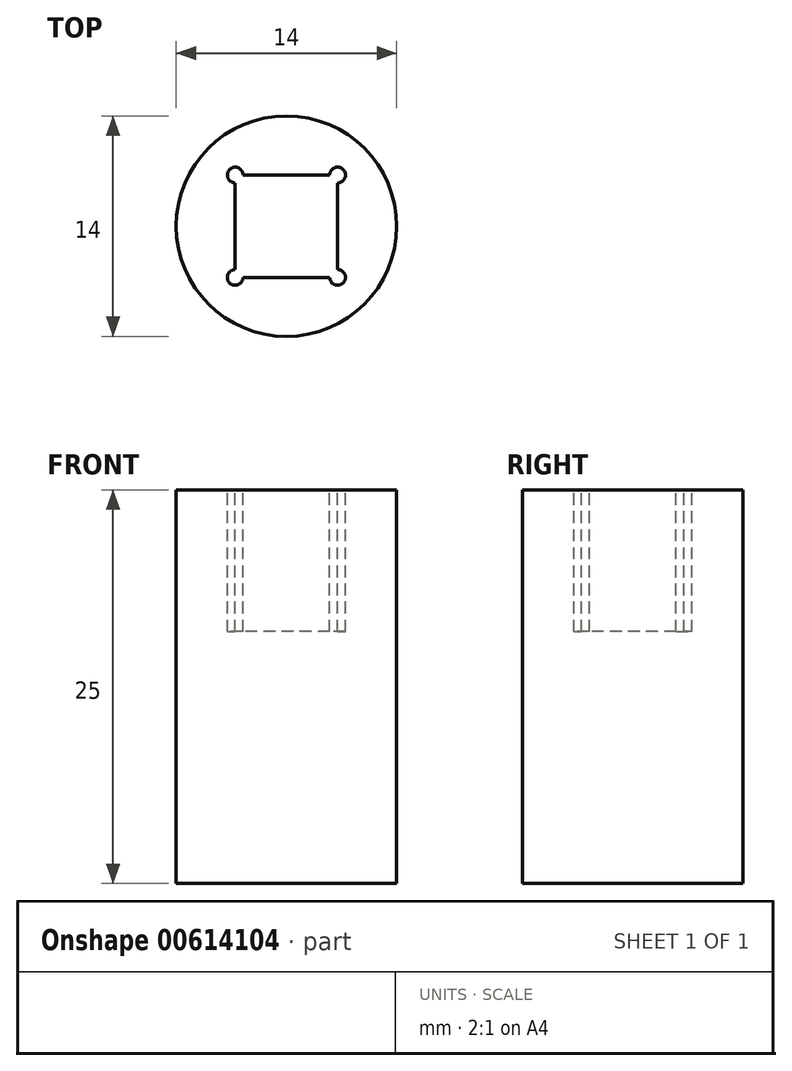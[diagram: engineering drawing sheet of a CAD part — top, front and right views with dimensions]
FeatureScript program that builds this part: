
annotation { "Feature Type Name" : "Feature", "Feature Type Description" : "" }
export const myFeature = defineFeature(function(context is Context, id is Id, definition is map)
    precondition{}
    {
        {
            var Q0;
            Q0=qCreatedBy(makeId("Top.planeOp"),FACE);
            var sketch = newSketch(context, id + "F0", { "sketchPlane" : qUnion([Q0])});
            skCircle(sketch, "E0", {"center": v(0, 0) * mm, "radius": 7 * mm});
            skSolve(sketch);
        }
        {
            var Q0;
            Q0=makeQuery(id+"F0.imprint","IMPRINT",FACE,{"disambiguationData":[TD([[makeQuery(id+"F0.imprint","IMPRINT",EDGE,{"derivedFrom":sQuery(id+"F0.wireOp",EDGE,"E0")}),1.0]])]});
            extrude(context, id + "F1", {"entities" : qUnion([Q0]), "depth" : 25 * mm, "offsetDistance" : 25 * mm});
        }
        {
            var Q0;
            Q0=makeQuery(id+"F1.opExtrude","CAP_FACE",FACE,{"disambiguationData":[OSD([sQuery(id+"F0.wireOp",EDGE,"E0")])],"isStart":false});
            var sketch = newSketch(context, id + "F2", { "sketchPlane" : qUnion([Q0])});
            skLineSegment(sketch, "E1.bottom", {"start": v(3.25, 3.25) * mm, "end": v(-3.25, 3.25) * mm});
            skLineSegment(sketch, "E1.top", {"start": v(3.25, -3.25) * mm, "end": v(-3.25, -3.25) * mm});
            skLineSegment(sketch, "E1.left", {"start": v(3.25, 3.25) * mm, "end": v(3.25, -3.25) * mm});
            skLineSegment(sketch, "E1.right", {"start": v(-3.25, 3.25) * mm, "end": v(-3.25, -3.25) * mm});
            skPoint(sketch, "E1.middle", {"position": v(0, 0) * mm});
            skCircle(sketch, "E2", {"center": v(-3.25, 3.25) * mm, "radius": 0.5 * mm});
            skCircle(sketch, "E3", {"center": v(3.25, 3.25) * mm, "radius": 0.5 * mm});
            skCircle(sketch, "E4", {"center": v(3.25, -3.25) * mm, "radius": 0.5 * mm});
            skCircle(sketch, "E5", {"center": v(-3.25, -3.25) * mm, "radius": 0.5 * mm});
            skSolve(sketch);
        }
        {
            var Q0;
            {var subQ5=sQuery(id+"F2.wireOp",EDGE,"E3");var subQ13=sQuery(id+"F2.wireOp",EDGE,"E1.bottom");var subQ14=makeQuery(id+"F2.imprint","INTERSECT",VERTEX,{"derivedFrom":[subQ13,subQ5]});Q0=makeQuery(id+"F2.imprint","IMPRINT",FACE,{"disambiguationData":[TD([[makeQuery(id+"F2.imprint","IMPRINT",EDGE,{"disambiguationData":[TD([[subQ14,-1.0]])],"derivedFrom":subQ13}),1.0]])]});}
            var Q1;
            {var subQ0=sQuery(id+"F2.wireOp",EDGE,"E1.right");var subQ1=sQuery(id+"F2.wireOp",EDGE,"E1.bottom");var subQ2=makeQuery(id+"F2.imprint","INTERSECT",VERTEX,{"derivedFrom":[subQ1,subQ0]});Q1=makeQuery(id+"F2.imprint","IMPRINT",FACE,{"disambiguationData":[TD([[makeQuery(id+"F2.imprint","IMPRINT",EDGE,{"disambiguationData":[TD([[subQ2,1.0]])],"derivedFrom":subQ1}),-1.0]])]});}
            var Q2;
            {var subQ0=sQuery(id+"F2.wireOp",EDGE,"E1.right");var subQ1=sQuery(id+"F2.wireOp",EDGE,"E1.top");var subQ2=makeQuery(id+"F2.imprint","INTERSECT",VERTEX,{"derivedFrom":[subQ1,subQ0]});Q2=makeQuery(id+"F2.imprint","IMPRINT",FACE,{"disambiguationData":[TD([[makeQuery(id+"F2.imprint","IMPRINT",EDGE,{"disambiguationData":[TD([[subQ2,1.0]])],"derivedFrom":subQ1}),1.0]])]});}
            var Q3;
            {var subQ0=sQuery(id+"F2.wireOp",EDGE,"E1.right");var subQ1=sQuery(id+"F2.wireOp",EDGE,"E1.top");var subQ2=makeQuery(id+"F2.imprint","INTERSECT",VERTEX,{"derivedFrom":[subQ1,subQ0]});Q3=makeQuery(id+"F2.imprint","IMPRINT",FACE,{"disambiguationData":[TD([[makeQuery(id+"F2.imprint","IMPRINT",EDGE,{"disambiguationData":[TD([[subQ2,1.0]])],"derivedFrom":subQ1}),-1.0]])]});}
            var Q4;
            {var subQ0=sQuery(id+"F2.wireOp",EDGE,"E1.right");var subQ1=sQuery(id+"F2.wireOp",EDGE,"E1.bottom");var subQ2=makeQuery(id+"F2.imprint","INTERSECT",VERTEX,{"derivedFrom":[subQ1,subQ0]});Q4=makeQuery(id+"F2.imprint","IMPRINT",FACE,{"disambiguationData":[TD([[makeQuery(id+"F2.imprint","IMPRINT",EDGE,{"disambiguationData":[TD([[subQ2,1.0]])],"derivedFrom":subQ1}),1.0]])]});}
            var Q5;
            {var subQ0=sQuery(id+"F2.wireOp",EDGE,"E1.left");var subQ1=sQuery(id+"F2.wireOp",EDGE,"E1.bottom");var subQ2=makeQuery(id+"F2.imprint","INTERSECT",VERTEX,{"derivedFrom":[subQ1,subQ0]});Q5=makeQuery(id+"F2.imprint","IMPRINT",FACE,{"disambiguationData":[TD([[makeQuery(id+"F2.imprint","IMPRINT",EDGE,{"disambiguationData":[TD([[subQ2,-1.0]])],"derivedFrom":subQ1}),1.0]])]});}
            var Q6;
            {var subQ0=sQuery(id+"F2.wireOp",EDGE,"E1.left");var subQ1=sQuery(id+"F2.wireOp",EDGE,"E1.bottom");var subQ2=makeQuery(id+"F2.imprint","INTERSECT",VERTEX,{"derivedFrom":[subQ1,subQ0]});Q6=makeQuery(id+"F2.imprint","IMPRINT",FACE,{"disambiguationData":[TD([[makeQuery(id+"F2.imprint","IMPRINT",EDGE,{"disambiguationData":[TD([[subQ2,-1.0]])],"derivedFrom":subQ1}),-1.0]])]});}
            var Q7;
            {var subQ0=sQuery(id+"F2.wireOp",EDGE,"E1.left");var subQ1=sQuery(id+"F2.wireOp",EDGE,"E1.top");var subQ2=makeQuery(id+"F2.imprint","INTERSECT",VERTEX,{"derivedFrom":[subQ1,subQ0]});Q7=makeQuery(id+"F2.imprint","IMPRINT",FACE,{"disambiguationData":[TD([[makeQuery(id+"F2.imprint","IMPRINT",EDGE,{"disambiguationData":[TD([[subQ2,-1.0]])],"derivedFrom":subQ1}),-1.0]])]});}
            var Q8;
            {var subQ0=sQuery(id+"F2.wireOp",EDGE,"E1.left");var subQ1=sQuery(id+"F2.wireOp",EDGE,"E1.top");var subQ2=makeQuery(id+"F2.imprint","INTERSECT",VERTEX,{"derivedFrom":[subQ1,subQ0]});Q8=makeQuery(id+"F2.imprint","IMPRINT",FACE,{"disambiguationData":[TD([[makeQuery(id+"F2.imprint","IMPRINT",EDGE,{"disambiguationData":[TD([[subQ2,-1.0]])],"derivedFrom":subQ1}),1.0]])]});}
            extrude(context, id + "F3", {"entities" : qUnion([Q0, Q1, Q2, Q3, Q4, Q5, Q6, Q7, Q8]), "operationType" : NewBodyOperationType.REMOVE, "oppositeDirection" : true, "depth" : 9 * mm, "offsetDistance" : 25 * mm});
        }
    });
